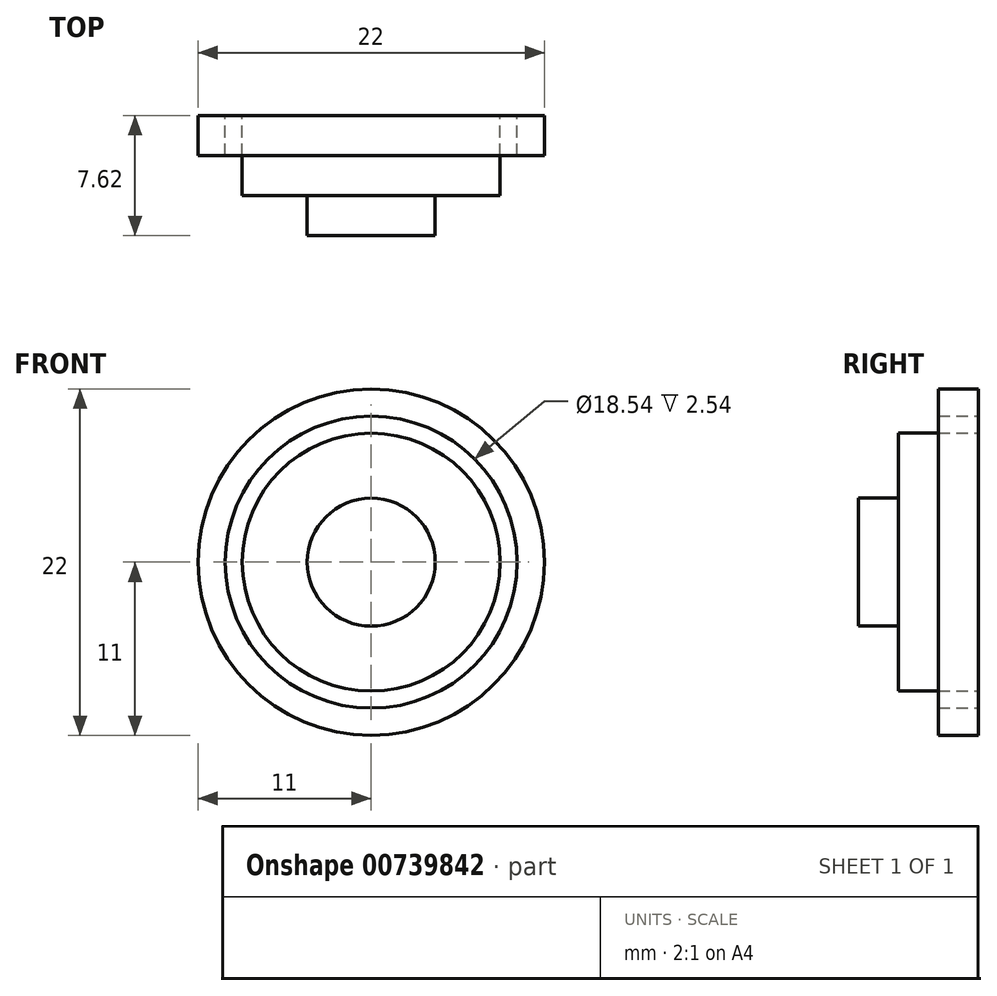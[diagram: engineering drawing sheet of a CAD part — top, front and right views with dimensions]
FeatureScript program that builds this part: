
annotation { "Feature Type Name" : "Feature", "Feature Type Description" : "" }
export const myFeature = defineFeature(function(context is Context, id is Id, definition is map)
    precondition{}
    {
        {
            var Q0;
            Q0=qCreatedBy(makeId("Front.planeOp"),FACE);
            var sketch = newSketch(context, id + "F0", { "sketchPlane" : qUnion([Q0])});
            skCircle(sketch, "E0", {"center": v(0, 0) * mm, "radius": 11 * mm});
            skCircle(sketch, "E1", {"center": v(0, 0) * mm, "radius": 9.27 * mm});
            skSolve(sketch);
        }
        {
            var Q0;
            Q0=qCreatedBy(makeId("Front.planeOp"),FACE);
            var sketch = newSketch(context, id + "F1", { "sketchPlane" : qUnion([Q0])});
            skCircle(sketch, "E2", {"center": v(0, 0) * mm, "radius": 4.06 * mm});
            skSolve(sketch);
        }
        {
            var Q0;
            Q0=makeQuery(id+"F1.imprint","IMPRINT",FACE,{"disambiguationData":[TD([[makeQuery(id+"F1.imprint","IMPRINT",EDGE,{"derivedFrom":sQuery(id+"F1.wireOp",EDGE,"E2")}),1.0]])]});
            extrude(context, id + "F2", {"entities" : qUnion([Q0]), "depth" : 7.62 * mm, "offsetDistance" : 25.4 * mm});
        }
        {
            var Q0;
            Q0=qCreatedBy(makeId("Front.planeOp"),FACE);
            var sketch = newSketch(context, id + "F3", { "sketchPlane" : qUnion([Q0])});
            skCircle(sketch, "E3", {"center": v(0, 0) * mm, "radius": 8.2 * mm});
            skSolve(sketch);
        }
        {
            var Q0;
            Q0=makeQuery(id+"F3.imprint","IMPRINT",FACE,{"disambiguationData":[TD([[makeQuery(id+"F3.imprint","IMPRINT",EDGE,{"derivedFrom":sQuery(id+"F3.wireOp",EDGE,"E3")}),1.0]])]});
            extrude(context, id + "F4", {"entities" : qUnion([Q0]), "operationType" : NewBodyOperationType.ADD, "depth" : 5.08 * mm, "offsetDistance" : 25.4 * mm});
        }
        {
            var Q0;
            Q0=makeQuery(id+"F0.imprint","IMPRINT",FACE,{"disambiguationData":[TD([[makeQuery(id+"F0.imprint","IMPRINT",EDGE,{"derivedFrom":sQuery(id+"F0.wireOp",EDGE,"E0")}),1.0]])]});
            extrude(context, id + "F5", {"entities" : qUnion([Q0]), "depth" : 2.54 * mm, "offsetDistance" : 25.4 * mm});
        }
    });
